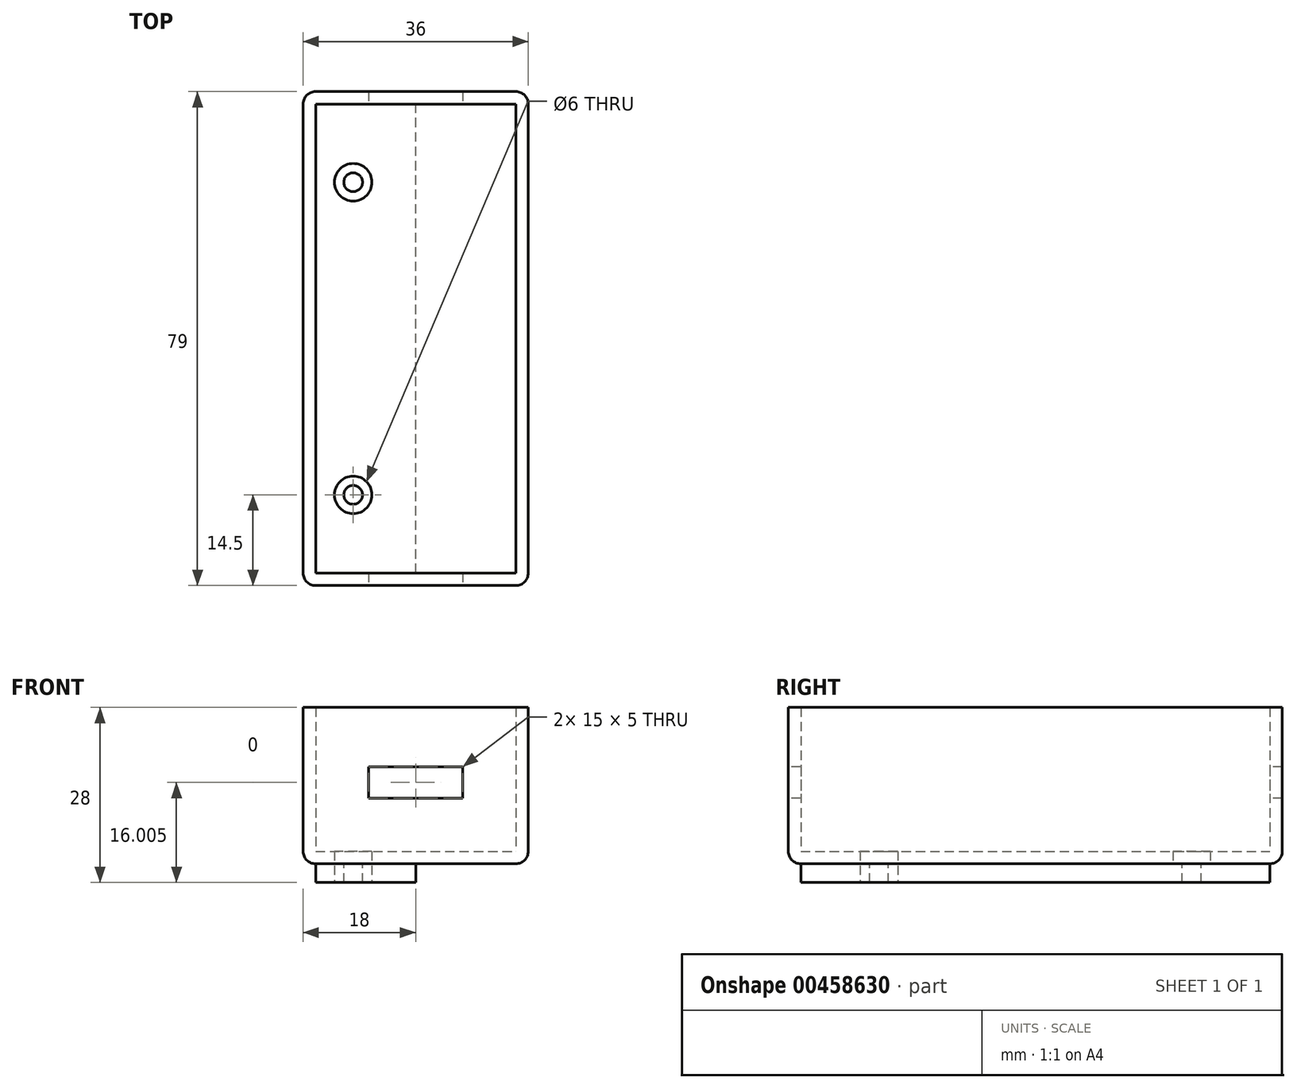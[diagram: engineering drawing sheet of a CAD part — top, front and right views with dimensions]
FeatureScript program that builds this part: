
annotation { "Feature Type Name" : "Feature", "Feature Type Description" : "" }
export const myFeature = defineFeature(function(context is Context, id is Id, definition is map)
    precondition{}
    {
        {
            var Q0;
            Q0=qCreatedBy(makeId("Top.planeOp"),FACE);
            var sketch = newSketch(context, id + "F0", { "sketchPlane" : qUnion([Q0])});
            skLineSegment(sketch, "E0.bottom", {"start": v(16, 37.5) * mm, "end": v(-16, 37.5) * mm});
            skLineSegment(sketch, "E0.top", {"start": v(16, -37.5) * mm, "end": v(-16, -37.5) * mm});
            skLineSegment(sketch, "E0.left", {"start": v(16, 37.5) * mm, "end": v(16, -37.5) * mm});
            skLineSegment(sketch, "E0.right", {"start": v(-16, 37.5) * mm, "end": v(-16, -37.5) * mm});
            skPoint(sketch, "E0.middle", {"position": v(0, 0) * mm});
            skLineSegment(sketch, "E1.0", {"start": v(18, 39.5) * mm, "end": v(-18, 39.5) * mm});
            skLineSegment(sketch, "E1.1", {"start": v(18, 39.5) * mm, "end": v(18, -39.5) * mm});
            skLineSegment(sketch, "E1.2", {"start": v(18, -39.5) * mm, "end": v(-18, -39.5) * mm});
            skLineSegment(sketch, "E1.3", {"start": v(-18, 39.5) * mm, "end": v(-18, -39.5) * mm});
            skCircle(sketch, "E2", {"center": v(-10, 25) * mm, "radius": 1.5 * mm});
            skCircle(sketch, "E3.MirrorC", {"center": v(-10, -25) * mm, "radius": 1.5 * mm});
            skLineSegment(sketch, "E4", {"start": v(0, -37.5) * mm, "end": v(0, 37.5) * mm});
            skCircle(sketch, "E5", {"center": v(-10, 25) * mm, "radius": 3 * mm});
            skCircle(sketch, "E6.MirrorC", {"center": v(-10, -25) * mm, "radius": 3 * mm});
            skSolve(sketch);
        }
        {
            var Q0;
            Q0 = qSketchRegion(id + "F0", true);
            var Q1;
            Q1=makeQuery(id+"F0.imprint","IMPRINT",FACE,{"disambiguationData":[TD([[makeQuery(id+"F0.imprint","IMPRINT",EDGE,{"derivedFrom":sQuery(id+"F0.wireOp",EDGE,"E0.bottom")}),1.0]])]});
            var Q2;
            {var subQ0=sQuery(id+"F0.wireOp",EDGE,"E0.right");Q2=makeQuery(id+"F0.imprint","IMPRINT",FACE,{"disambiguationData":[TD([[makeQuery(id+"F0.imprint","IMPRINT",EDGE,{"derivedFrom":subQ0}),1.0]])]});}
            extrude(context, id + "F1", {"entities" : qUnion([Q0, Q1, Q2]), "depth" : 2 * mm});
        }
        {
            var Q0;
            Q0=makeQuery(id+"F0.imprint","IMPRINT",FACE,{"disambiguationData":[TD([[makeQuery(id+"F0.imprint","IMPRINT",EDGE,{"derivedFrom":sQuery(id+"F0.wireOp",EDGE,"E0.bottom")}),-1.0]])]});
            extrude(context, id + "F2", {"entities" : qUnion([Q0]), "operationType" : NewBodyOperationType.ADD, "depth" : 25 * mm});
        }
        {
            var Q0;
            {var subQ0=sQuery(id+"F0.wireOp",EDGE,"E0.right");Q0=makeQuery(id+"F0.imprint","IMPRINT",FACE,{"disambiguationData":[TD([[makeQuery(id+"F0.imprint","IMPRINT",EDGE,{"derivedFrom":subQ0}),1.0]])]});}
            var Q1;
            Q1=makeQuery(id+"F0.imprint","IMPRINT",FACE,{"disambiguationData":[TD([[makeQuery(id+"F0.imprint","IMPRINT",EDGE,{"derivedFrom":sQuery(id+"F0.wireOp",EDGE,"E2")}),-1.0]])]});
            var Q2;
            Q2=makeQuery(id+"F0.imprint","IMPRINT",FACE,{"disambiguationData":[TD([[makeQuery(id+"F0.imprint","IMPRINT",EDGE,{"derivedFrom":sQuery(id+"F0.wireOp",EDGE,"E3.MirrorC")}),1.0]])]});
            extrude(context, id + "F3", {"entities" : qUnion([Q0, Q1, Q2]), "operationType" : NewBodyOperationType.ADD, "oppositeDirection" : true, "depth" : 3 * mm});
        }
        {
            var Q0;
            Q0=makeQuery(id+"F1.opExtrude","CAP_EDGE",EDGE,{"disambiguationData":[OSD([sQuery(id+"F0.wireOp",EDGE,"E1.3")])],"isStart":true});
            var Q1;
            Q1=makeQuery(id+"F1.opExtrude","CAP_EDGE",EDGE,{"disambiguationData":[OSD([sQuery(id+"F0.wireOp",EDGE,"E1.2")])],"isStart":true});
            var Q2;
            Q2=makeQuery(id+"F1.opExtrude","CAP_EDGE",EDGE,{"disambiguationData":[OSD([sQuery(id+"F0.wireOp",EDGE,"E1.0")])],"isStart":true});
            var Q3;
            Q3=makeQuery(id+"F1.opExtrude","CAP_EDGE",EDGE,{"disambiguationData":[OSD([sQuery(id+"F0.wireOp",EDGE,"E1.1")])],"isStart":true});
            var Q4;
            {var subQ0=sQuery(id+"F0.wireOp",EDGE,"E1.1");var subQ1=sQuery(id+"F0.wireOp",EDGE,"E1.0");Q4=makeQuery(id+"F2.boolean.opBoolean","MERGE",EDGE,{"derivedFrom":[makeQuery(id+"F1.opExtrude","SWEPT_EDGE",EDGE,{"disambiguationData":[OSD([subQ1,subQ0])]}),makeQuery(id+"F2.opExtrude","SWEPT_EDGE",EDGE,{"disambiguationData":[OSD([subQ1,subQ0])]})]});}
            var Q5;
            {var subQ0=sQuery(id+"F0.wireOp",EDGE,"E1.3");var subQ1=sQuery(id+"F0.wireOp",EDGE,"E1.0");Q5=makeQuery(id+"F2.boolean.opBoolean","MERGE",EDGE,{"derivedFrom":[makeQuery(id+"F1.opExtrude","SWEPT_EDGE",EDGE,{"disambiguationData":[OSD([subQ1,subQ0])]}),makeQuery(id+"F2.opExtrude","SWEPT_EDGE",EDGE,{"disambiguationData":[OSD([subQ1,subQ0])]})]});}
            var Q6;
            {var subQ0=sQuery(id+"F0.wireOp",EDGE,"E1.3");var subQ1=sQuery(id+"F0.wireOp",EDGE,"E1.2");Q6=makeQuery(id+"F2.boolean.opBoolean","MERGE",EDGE,{"derivedFrom":[makeQuery(id+"F1.opExtrude","SWEPT_EDGE",EDGE,{"disambiguationData":[OSD([subQ1,subQ0])]}),makeQuery(id+"F2.opExtrude","SWEPT_EDGE",EDGE,{"disambiguationData":[OSD([subQ1,subQ0])]})]});}
            var Q7;
            {var subQ0=sQuery(id+"F0.wireOp",EDGE,"E1.2");var subQ1=sQuery(id+"F0.wireOp",EDGE,"E1.1");Q7=makeQuery(id+"F2.boolean.opBoolean","MERGE",EDGE,{"derivedFrom":[makeQuery(id+"F1.opExtrude","SWEPT_EDGE",EDGE,{"disambiguationData":[OSD([subQ1,subQ0])]}),makeQuery(id+"F2.opExtrude","SWEPT_EDGE",EDGE,{"disambiguationData":[OSD([subQ1,subQ0])]})]});}
            fillet(context, id + "F4", {"entities" : qUnion([Q0, Q1, Q2, Q3, Q4, Q5, Q6, Q7]), "radius" : 2 * mm, "tangentPropagation" : true, "allowEdgeOverflow" : false});
        }
        {
            var Q0;
            {var subQ0=sQuery(id+"F0.wireOp",EDGE,"E1.2");Q0=makeQuery(id+"F2.boolean.opBoolean","MERGE",FACE,{"derivedFrom":[makeQuery(id+"F1.opExtrude","SWEPT_FACE",FACE,{"disambiguationData":[OSD([subQ0])]}),makeQuery(id+"F2.opExtrude","SWEPT_FACE",FACE,{"disambiguationData":[OSD([subQ0])]})]});}
            var sketch = newSketch(context, id + "F5", { "sketchPlane" : qUnion([Q0])});
            skLineSegment(sketch, "E7.bottom", {"start": v(7.5, 15.5) * mm, "end": v(-7.5, 15.5) * mm});
            skLineSegment(sketch, "E7.top", {"start": v(7.5, 10.5) * mm, "end": v(-7.5, 10.5) * mm});
            skLineSegment(sketch, "E7.left", {"start": v(7.5, 15.5) * mm, "end": v(7.5, 10.5) * mm});
            skLineSegment(sketch, "E7.right", {"start": v(-7.5, 15.5) * mm, "end": v(-7.5, 10.5) * mm});
            skPoint(sketch, "E7.middle", {"position": v(0, 13) * mm});
            skSolve(sketch);
        }
        {
            var Q0;
            Q0=makeQuery(id+"F5.imprint","IMPRINT",FACE,{"disambiguationData":[TD([[makeQuery(id+"F5.imprint","IMPRINT",EDGE,{"derivedFrom":sQuery(id+"F5.wireOp",EDGE,"E7.bottom")}),1.0]])]});
            extrude(context, id + "F6", {"entities" : qUnion([Q0]), "operationType" : NewBodyOperationType.REMOVE, "oppositeDirection" : true, "depth" : 100 * mm});
        }
    });
